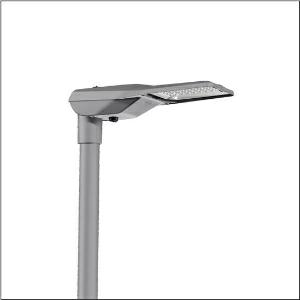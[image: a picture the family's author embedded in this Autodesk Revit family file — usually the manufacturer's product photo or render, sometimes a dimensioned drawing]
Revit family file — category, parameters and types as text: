
# Revit family: streetlight_sl_21_iq_mini___st1_0a_5xe2d41y08gb_5b29
name_source: partatom
category: Lighting Fixtures
units: mm (PartAtom-declared; Revit-internal decimal feet)

## family parameters
Cut with Voids When Loaded = No
Host = Face
Light Source = No
Part Type = Normal
Room Calculation Point = No
Round Connector Dimension = Use Diameter
Shared = No

## types (1)
- --- (1 x LED, 6190 lm, 39.8 W, 4000K)
    Apparent Load = 40 VA
    CIE Flux Codes = 37 72 97 100 100
    Color Rendering = 70
    Color Temperature = 4000K
    Default Elevation = 1800 mm
    Description = Streetlight SL 21 iQ mini, mast luminaire, primary light control with lens, of PMMA, primary optical cover: cover, of toughened safety glass, transparent, light distribution: ST1.0a, light emission: direct distribution, primary light characteristic: asymmetric, installation type: post-top, side-entry, LED, High Power LED, rated luminous flux: 6.190lm, luminous efficacy: 156lm/W, light colour: 740, colour temperature: 4000K, control: pre-setting: logarithmic dimming characteristic, Street-Remote, Auto-Match, Temp-Guard, Lumen-Switch, Night-Set, Smart-Wire, Light-Fading, Desk-Remote (wireless, voltage-free reading and setting of iQ features in the workshop via application-optimized NFC function/RFID function), optimised constant luminous flux control (CLO 2.0), mains connection: 220..240V, AC, 50/60Hz, start of lifetime: 40W, end of service life: 41W, reduction: 18W, luminaire housing, of diecast aluminium, powder-coated, Siteco® metallic grey (DB 702S), corrosivity category C5 mid according to DIN EN ISO 12944, please order mast flange separately, inclination adjustable: 0°, 5°, 10°, 15°, sealing non-destructively replaceable, multi-level sealing system, length: 628mm, width: 235mm, height: 110mm, mast flange for spigot size: 42mm (side-entry): 5XC10008XM4, 60/48mm (side-entry/post-top): 5XC10108XM2, 76/60mm (side-entry/post-top): 5XC10108XM1, Smart Interface below and above, protection rating (complete): IP66, insulation class (complete): insulation class II (safety insulation), certification: CE, ENEC, ENEC+, VDE, impact resistance: IK09, permissible operating ambient temperature for outdoor applications: -40..+50°C, standard-compliant lighting for roads and squares, packaging unit: 1 piece

Light Distribution: ST1.0a
    Height = 110 mm
    Lamp = 1 x LED
    Lamp Light Flux = 6190 lm
    Lamp Power = 39.8 W
    Lamp count = 1
    Length = 625 mm
    Luminous efficacy = 156 lm/W
    Manufacturer = Siteco
    ModVariant = No
    Model = 5XE2D41Y08GB
    Number of Poles = 1
    OnlyDefault = Yes
    Power Factor = 1
    Product Name = Streetlight SL 21 iQ mini | ST1.0a
    Product group = mast luminaire | pylon top
    ProductGroupID = 6100
    Protection Class = Protection class II
    Protection Degree = IP 66
    RLX_Detail_Level = 1
    RLX_Emergency_Light_Flux = 0 lm
    RLX_Emergency_Type = 0
    RLX_Emergency_Type_DB = No
    RlxData = <blob elided: 94045 chars, md5=af17791f>
    Socket = socket
    Standby Power = 0 W
    System Light Flux = 6190 lm
    System Power = 40 W
    Type Comments = factory setting: luminous flux: 100 % | dim-lin: 254 | 800 mA
    Type Image = l_1003514.jpg
    URL = http://relux.com
    VarID = @adj_083605
    Voltage = 0 V
    Weight = 0.00 kg
    Width = 234 mm

## geometry (parser evidence)
native form markers: Blend x4, Sweep x10
no freeform markers — native parametric forms only
